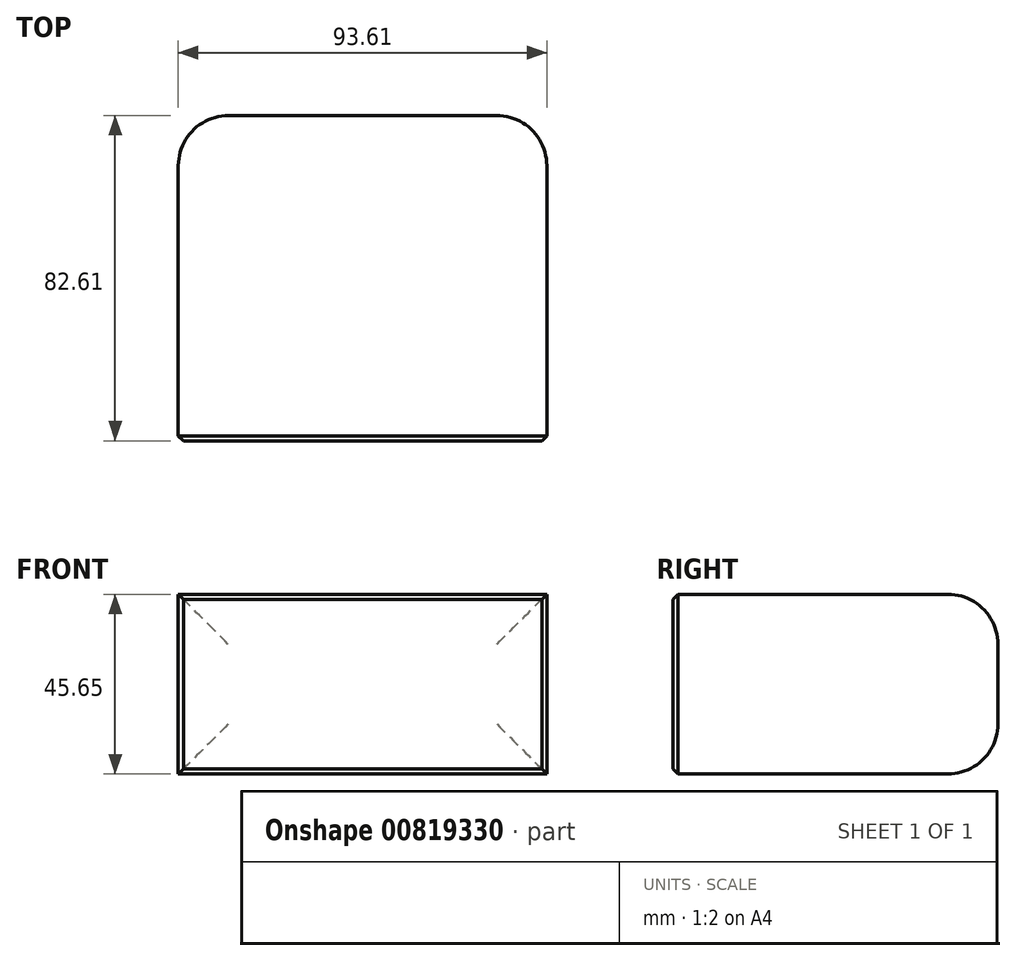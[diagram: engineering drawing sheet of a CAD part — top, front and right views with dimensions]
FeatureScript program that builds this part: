
annotation { "Feature Type Name" : "Feature", "Feature Type Description" : "" }
export const myFeature = defineFeature(function(context is Context, id is Id, definition is map)
    precondition{}
    {
        {
            var Q0;
            Q0=qCreatedBy(makeId("Top.planeOp"),FACE);
            var sketch = newSketch(context, id + "F0", { "sketchPlane" : qUnion([Q0])});
            skLineSegment(sketch, "E0.bottom", {"start": v(-43.5, 39.35) * mm, "end": v(50.1, 39.35) * mm});
            skLineSegment(sketch, "E0.top", {"start": v(-43.5, -43.26) * mm, "end": v(50.1, -43.26) * mm});
            skLineSegment(sketch, "E0.left", {"start": v(-43.5, 39.35) * mm, "end": v(-43.5, -43.26) * mm});
            skLineSegment(sketch, "E0.right", {"start": v(50.1, 39.35) * mm, "end": v(50.1, -43.26) * mm});
            skSolve(sketch);
        }
        {
            var Q0;
            Q0=makeQuery(id+"F0.imprint","IMPRINT",FACE,{"disambiguationData":[TD([[makeQuery(id+"F0.imprint","IMPRINT",EDGE,{"derivedFrom":sQuery(id+"F0.wireOp",EDGE,"E0.bottom")}),-1.0]])]});
            extrude(context, id + "F1", {"entities" : qUnion([Q0]), "depth" : 45.65 * mm, "offsetDistance" : 25.4 * mm});
        }
        {
            var Q0;
            Q0=makeQuery(id+"F1.opExtrude","SWEPT_FACE",FACE,{"disambiguationData":[OSD([sQuery(id+"F0.wireOp",EDGE,"E0.top")])]});
            chamfer(context, id + "F2", {"entities" : qUnion([Q0]), "width" : 1.27 * mm, "tangentPropagation" : true});
        }
        {
            var Q0;
            Q0=makeQuery(id+"F1.opExtrude","SWEPT_FACE",FACE,{"disambiguationData":[OSD([sQuery(id+"F0.wireOp",EDGE,"E0.bottom")])]});
            fillet(context, id + "F3", {"entities" : qUnion([Q0]), "radius" : 12.7 * mm, "tangentPropagation" : true, "allowEdgeOverflow" : false});
        }
    });
